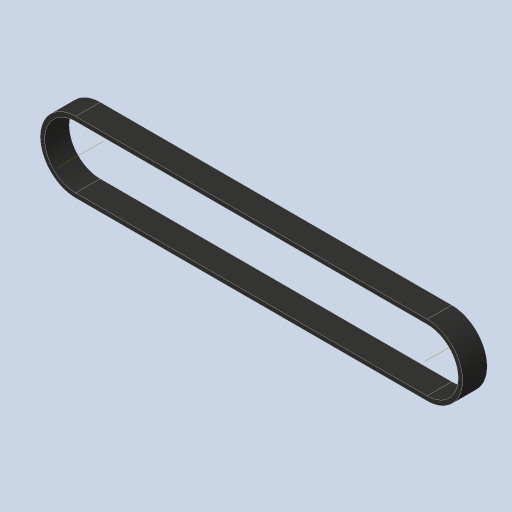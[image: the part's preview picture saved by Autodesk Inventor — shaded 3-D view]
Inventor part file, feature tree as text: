
AUTODESK INVENTOR PART (.ipt)
format: ipt  version: 2023.4 (Build 274418000, 418)  size: 162,304 bytes
history: native  units: in
note: dims shown in document units (in); Inventor stores cm internally (conversion verified against a paired STEP export)
features: sketch x3, extrude x1, other x1, projected_geometry x1
ambient origin geometry x8: Origin, YZ Plane, XZ Plane, XY Plane, X Axis, Y Axis, Z Axis, Center Point
bodies: Body1 (feature_tree)
feature tree (6):
  sketch  "Sketch2"  dims[d0=0.9023in d1=0.9023in]
  extrude  "Extrusion2"  Depth=0.9023in
  sketch  "Sketch5"  dims[d3=1.4174in d5=4.7834in d9=0.0787in d10=0.0598in d11=0.0299in d12=0.0219in d13=0.0219in d14=0.0059in d15=0.0059in d20=0.3346in d21=0.0in d22=0.0787in d23=0.0598in d24=0.0299in d25=0.0219in d26=0.0219in d27=0.0059in d28=0.0059in d29=0.0299in d30=0.0394in d31=0.0787in d32=0.0232in d34=0.0219in d35=0.0in d36=0.0in d37=0.0059in d38=0.0022in d39=0.0022in d40=0.0in d41=0.0in d42=0.0081in d43=0.0081in d44=0.0299in]
  other  "Work Axis1"
  sketch  "Sketch4"  dims[d2=1.4174in]
  projected_geometry  "Projected Loop1"
